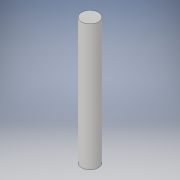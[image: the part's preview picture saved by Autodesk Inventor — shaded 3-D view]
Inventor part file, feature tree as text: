
AUTODESK INVENTOR PART (.ipt)
format: ipt  version: 2019 (Build 230136000, 136)  size: 88,064 bytes
history: native  units: mm
features: extrude x1, sketch x1
ambient origin geometry x8: Origin, YZ Plane, XZ Plane, XY Plane, X Axis, Y Axis, Z Axis, Center Point
bodies: Solid1 (feature_tree)
feature tree (2):
  extrude  "Extrusion1"  Depth=75.0mm TaperAngle=0.0deg
  sketch  "Sketch1"  dims[d0=10.0mm d1=75.0mm d2=0.0mm]
